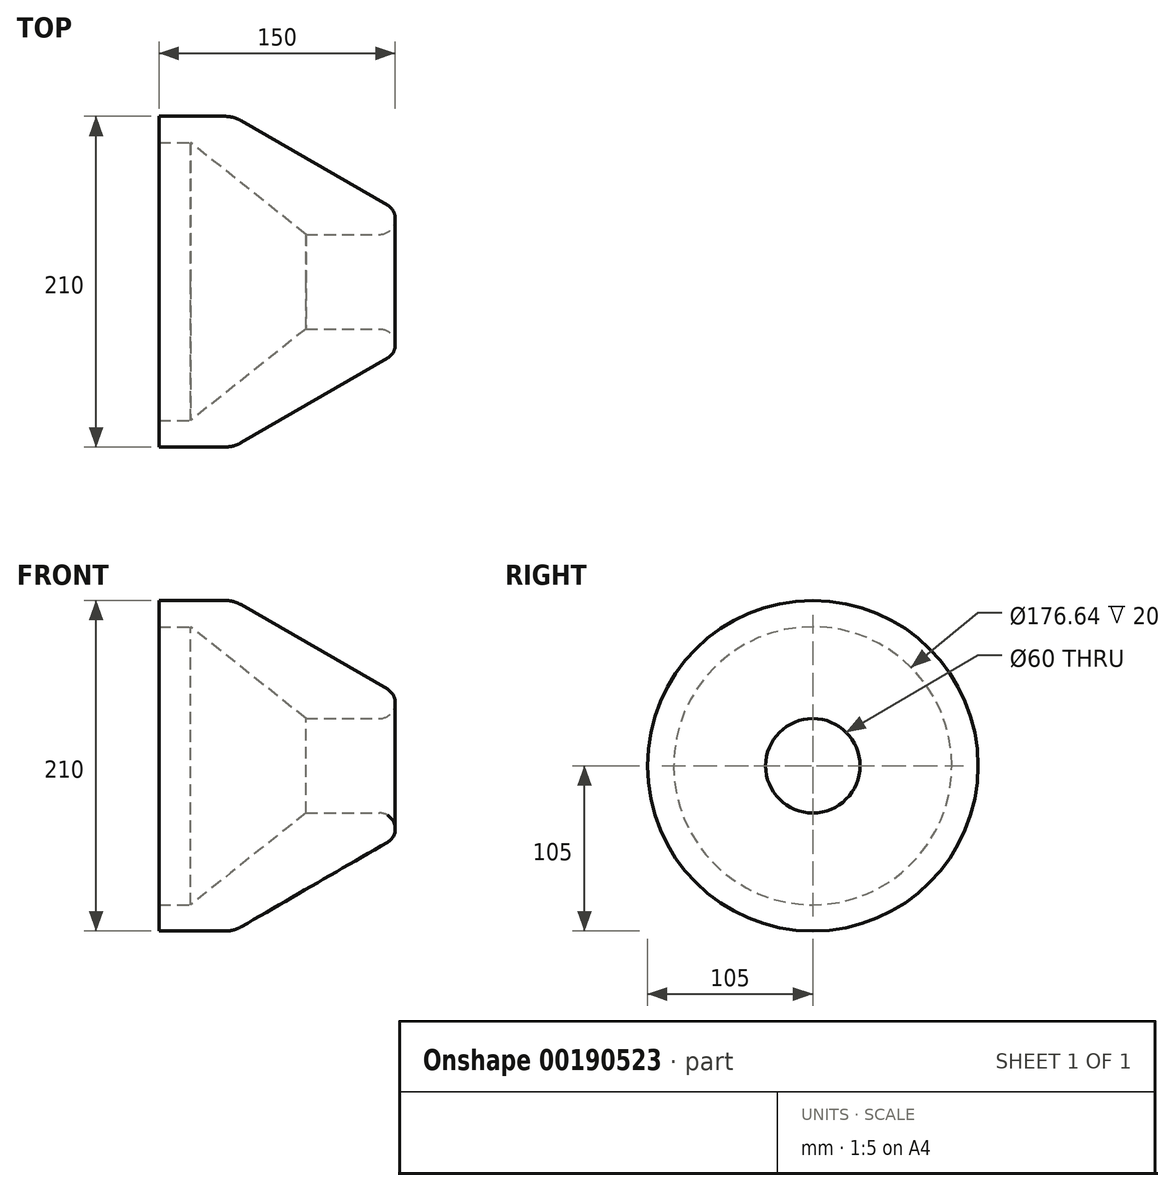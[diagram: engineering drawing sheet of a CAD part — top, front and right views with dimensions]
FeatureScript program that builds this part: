
annotation { "Feature Type Name" : "Feature", "Feature Type Description" : "" }
export const myFeature = defineFeature(function(context is Context, id is Id, definition is map)
    precondition{}
    {
        {
            var Q0;
            Q0=qCreatedBy(makeId("Front.planeOp"),FACE);
            var sketch = newSketch(context, id + "F0", { "sketchPlane" : qUnion([Q0])});
            skLineSegment(sketch, "E0.bottom", {"start": v(-75, 105) * mm, "end": v(-32.94, 105) * mm});
            skLineSegment(sketch, "E0.left", {"start": v(-75, 105) * mm, "end": v(-75, 88.32) * mm});
            skLineSegment(sketch, "E0.right", {"start": v(75, 42.5) * mm, "end": v(75, 40) * mm});
            skPoint(sketch, "E0.middle", {"position": v(0, 0) * mm});
            skLineSegment(sketch, "E1", {"start": v(96.93, 0) * mm, "end": v(-171.76, 0) * mm});
            skLineSegment(sketch, "E2", {"start": v(65, 30) * mm, "end": v(18.32, 30) * mm});
            skArc(sketch, "E3", {"start": v(65, 30) * mm, "mid": v(74.66, 37.41) * mm, "end": v(70, 48.66) * mm});
            skLineSegment(sketch, "E4", {"start": v(70, 48.66) * mm, "end": v(-22.94, 102.32) * mm});
            skArc(sketch, "E5.filletArc", {"start": v(-22.94, 102.32) * mm, "mid": v(-27.77, 104.32) * mm, "end": v(-32.94, 105) * mm});
            skLineSegment(sketch, "E6", {"start": v(-75, 88.32) * mm, "end": v(-55, 88.32) * mm});
            skLineSegment(sketch, "E7", {"start": v(-55, 88.32) * mm, "end": v(18.32, 30) * mm});
            skPoint(sketch, "E0.top.end.orphan", {"position": v(75, -105) * mm});
            skSolve(sketch);
        }
        {
            var Q0;
            Q0=makeQuery(id+"F0.imprint","IMPRINT",FACE,{"disambiguationData":[TD([[makeQuery(id+"F0.imprint","IMPRINT",EDGE,{"derivedFrom":sQuery(id+"F0.wireOp",EDGE,"E0.bottom")}),-1.0]])]});
            var Q1;
            Q1=sQuery(id+"F0.wireOp",EDGE,"E1");
            revolve(context, id + "F1", {"entities" : qUnion([Q0]), "axis" : qUnion([Q1]), "revolveType" : RevolveType.FULL});
        }
    });
